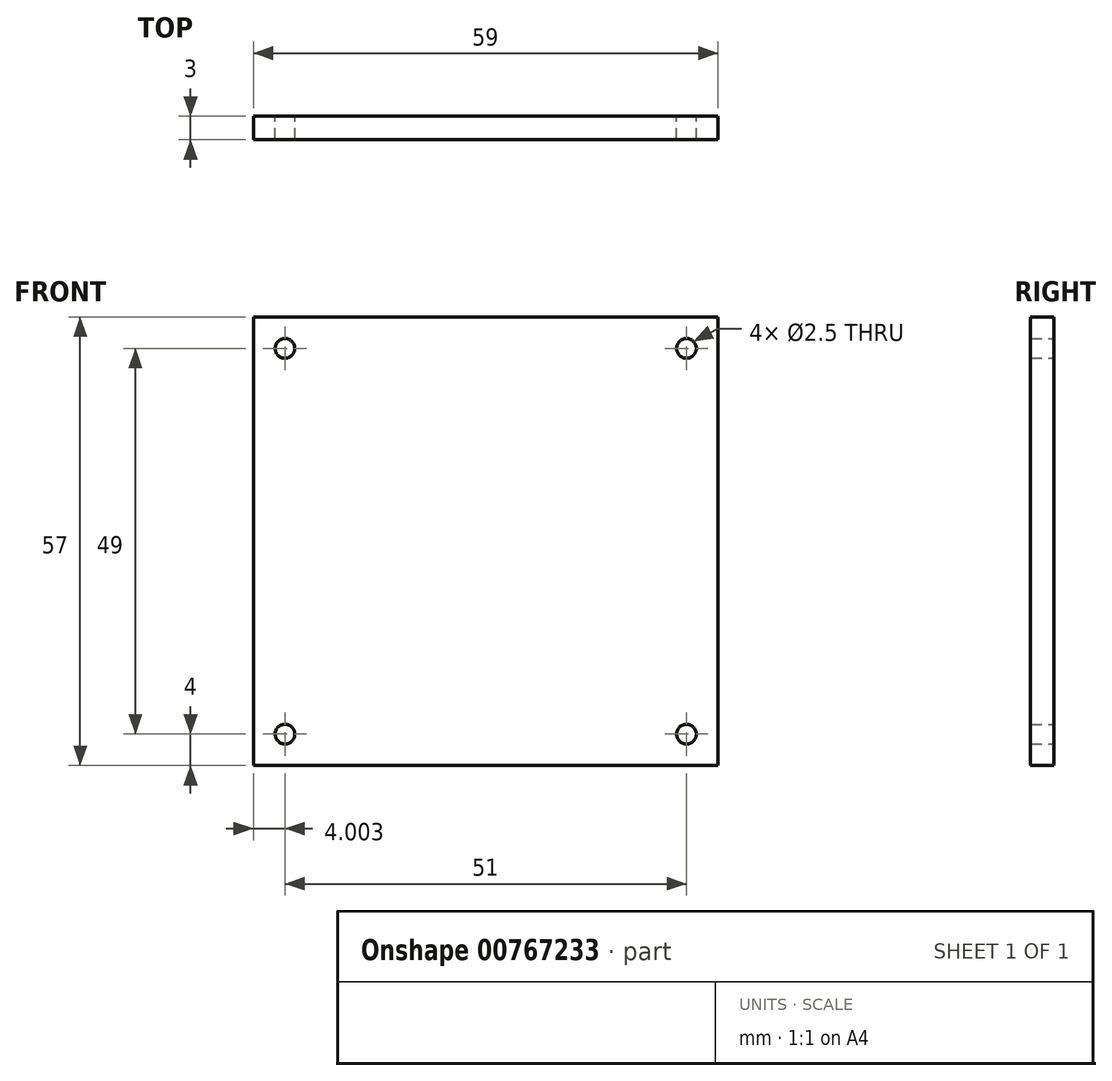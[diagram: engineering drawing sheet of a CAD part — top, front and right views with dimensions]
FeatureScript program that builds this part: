
annotation { "Feature Type Name" : "Feature", "Feature Type Description" : "" }
export const myFeature = defineFeature(function(context is Context, id is Id, definition is map)
    precondition{}
    {
        {
            var Q0;
            Q0=qCreatedBy(makeId("Front.planeOp"),FACE);
            var sketch = newSketch(context, id + "F0", { "sketchPlane" : qUnion([Q0])});
            skLineSegment(sketch, "E0.bottom", {"start": v(29.33, 57) * mm, "end": v(-29.67, 57) * mm});
            skLineSegment(sketch, "E0.top", {"start": v(29.33, 0) * mm, "end": v(-29.67, 0) * mm});
            skLineSegment(sketch, "E0.left", {"start": v(29.33, 57) * mm, "end": v(29.33, 0) * mm});
            skLineSegment(sketch, "E0.right", {"start": v(-29.67, 57) * mm, "end": v(-29.67, 0) * mm});
            skCircle(sketch, "E1", {"center": v(25.33, 53) * mm, "radius": 1.25 * mm});
            skCircle(sketch, "E2", {"center": v(-25.67, 53) * mm, "radius": 1.25 * mm});
            skCircle(sketch, "E3", {"center": v(25.33, 4) * mm, "radius": 1.25 * mm});
            skCircle(sketch, "E4", {"center": v(-25.67, 4) * mm, "radius": 1.25 * mm});
            skLineSegment(sketch, "E5.bottom", {"start": v(-27.67, 55) * mm, "end": v(27.33, 55) * mm});
            skLineSegment(sketch, "E5.top", {"start": v(-27.67, 2) * mm, "end": v(27.33, 2) * mm});
            skLineSegment(sketch, "E5.left", {"start": v(-27.67, 55) * mm, "end": v(-27.67, 2) * mm});
            skLineSegment(sketch, "E5.right", {"start": v(27.33, 55) * mm, "end": v(27.33, 2) * mm});
            skSolve(sketch);
        }
        {
            var Q0;
            Q0=makeQuery(id+"F0.imprint","IMPRINT",FACE,{"disambiguationData":[TD([[makeQuery(id+"F0.imprint","IMPRINT",EDGE,{"derivedFrom":sQuery(id+"F0.wireOp",EDGE,"E0.bottom")}),1.0]])]});
            var Q1;
            Q1=makeQuery(id+"F0.imprint","IMPRINT",FACE,{"disambiguationData":[TD([[makeQuery(id+"F0.imprint","IMPRINT",EDGE,{"derivedFrom":sQuery(id+"F0.wireOp",EDGE,"E1")}),-1.0]])]});
            extrude(context, id + "F1", {"entities" : qUnion([Q0, Q1]), "depth" : 3 * mm, "offsetDistance" : 25 * mm});
        }
    });
